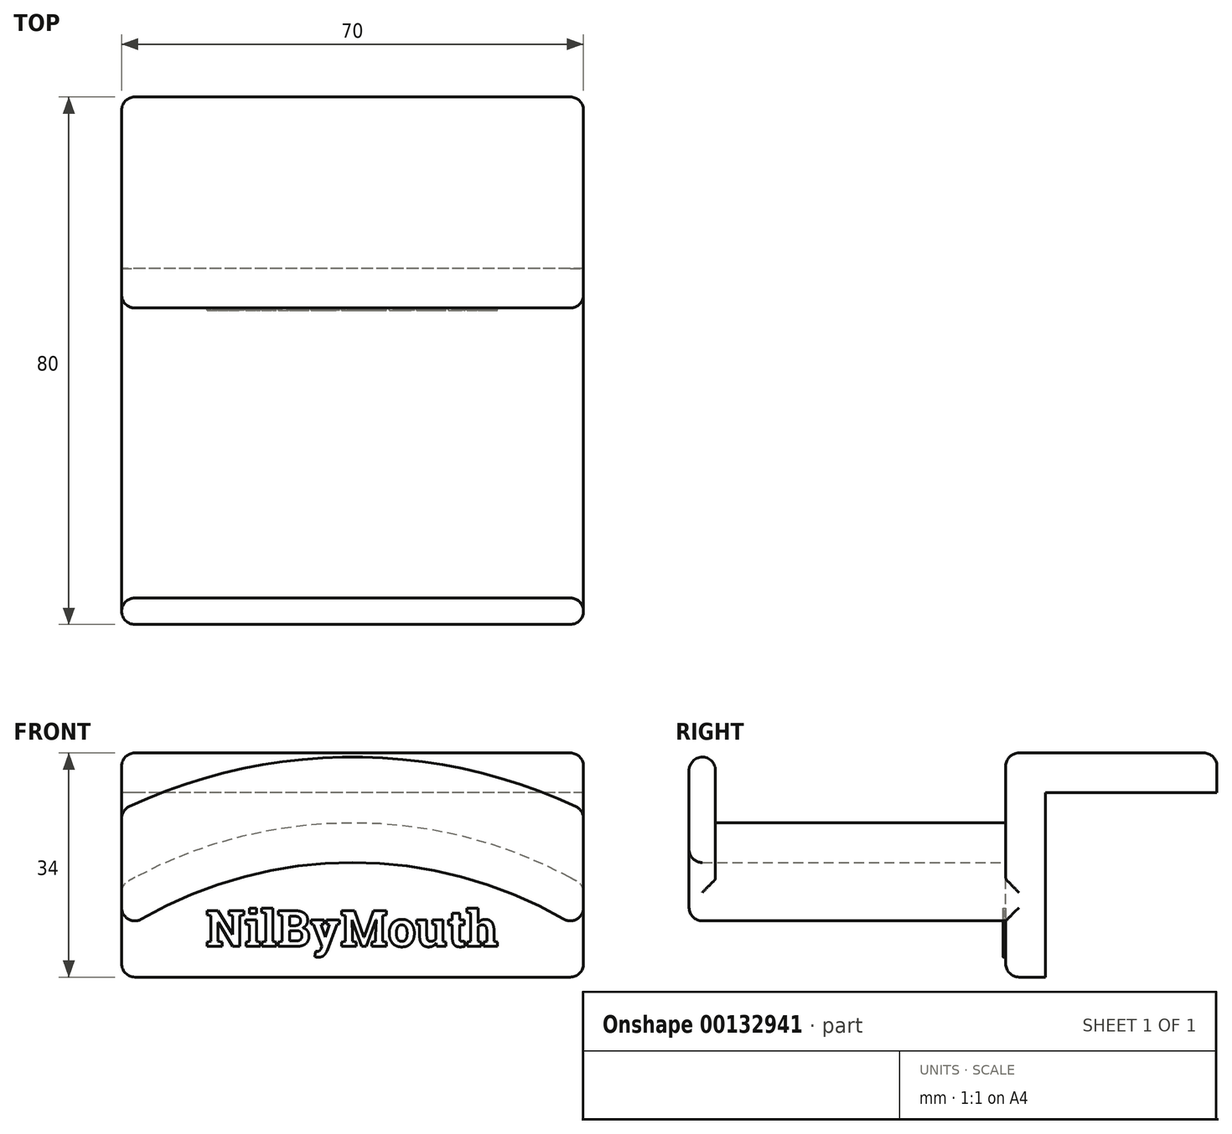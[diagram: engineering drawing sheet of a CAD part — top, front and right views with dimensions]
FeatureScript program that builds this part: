
annotation { "Feature Type Name" : "Feature", "Feature Type Description" : "" }
export const myFeature = defineFeature(function(context is Context, id is Id, definition is map)
    precondition{}
    {
        {
            var Q0;
            Q0=qCreatedBy(makeId("Front.planeOp"),FACE);
            var sketch = newSketch(context, id + "F0", { "sketchPlane" : qUnion([Q0])});
            skLineSegment(sketch, "E0.top", {"start": v(70, 0) * mm, "end": v(0, 0) * mm});
            skLineSegment(sketch, "E0.left", {"start": v(70, 14) * mm, "end": v(70, 0) * mm});
            skLineSegment(sketch, "E0.right", {"start": v(0, 14) * mm, "end": v(0, 0) * mm});
            skArc(sketch, "E1", {"start": v(70, 14) * mm, "mid": v(35, 23.38) * mm, "end": v(0, 14) * mm});
            skArc(sketch, "E2.0", {"start": v(70, 6.96) * mm, "mid": v(35, 17.38) * mm, "end": v(0, 6.96) * mm});
            skLineSegment(sketch, "E3.top", {"start": v(0, 34) * mm, "end": v(70, 34) * mm});
            skLineSegment(sketch, "E3.left", {"start": v(0, 14) * mm, "end": v(0, 34) * mm});
            skLineSegment(sketch, "E3.right", {"start": v(70, 14) * mm, "end": v(70, 34) * mm});
            skSolve(sketch);
        }
        {
            var Q0;
            Q0 = qSketchRegion(id + "F0", true);
            extrude(context, id + "F1", {"entities" : qUnion([Q0]), "depth" : 6 * mm});
        }
        {
            var Q0;
            {var subQ0=sQuery(id+"F0.wireOp",EDGE,"E1");Q0=makeQuery(id+"F0.imprint","IMPRINT",FACE,{"disambiguationData":[TD([[makeQuery(id+"F0.imprint","IMPRINT",EDGE,{"derivedFrom":subQ0}),1.0]])]});}
            extrude(context, id + "F2", {"entities" : qUnion([Q0]), "operationType" : NewBodyOperationType.ADD, "depth" : 50 * mm});
        }
        {
            var Q0;
            Q0=makeQuery(id+"F2.opExtrude","CAP_FACE",FACE,{"disambiguationData":[OSD([sQuery(id+"F0.wireOp",EDGE,"E0.left"),sQuery(id+"F0.wireOp",EDGE,"E0.right"),sQuery(id+"F0.wireOp",EDGE,"E1"),sQuery(id+"F0.wireOp",EDGE,"E2.0")])],"isStart":false});
            var sketch = newSketch(context, id + "F3", { "sketchPlane" : qUnion([Q0])});
            skArc(sketch, "E4.0", {"start": v(70, 25.32) * mm, "mid": v(35, 33.38) * mm, "end": v(0, 25.32) * mm});
            skLineSegment(sketch, "E5", {"start": v(0, 14) * mm, "end": v(0, 25.32) * mm});
            skLineSegment(sketch, "E6", {"start": v(70, 14) * mm, "end": v(70, 25.32) * mm});
            skSolve(sketch);
        }
        {
            var Q0;
            Q0 = qSketchRegion(id + "F3", true);
            var Q1;
            Q1=makeQuery(id+"F3.imprint","IMPRINT",FACE,{"disambiguationData":[TD([[makeQuery(id+"F3.imprint","IMPRINT",EDGE,{"derivedFrom":makeQuery(id+"F2.opExtrude","CAP_EDGE",EDGE,{"disambiguationData":[OSD([sQuery(id+"F0.wireOp",EDGE,"E0.left")])],"isStart":false})}),-1.0]])]});
            var Q2;
            Q2=makeQuery(id+"F3.imprint","IMPRINT",FACE,{"disambiguationData":[TD([[makeQuery(id+"F3.imprint","IMPRINT",EDGE,{"derivedFrom":sQuery(id+"F3.wireOp",EDGE,"E4.0")}),1.0]])]});
            extrude(context, id + "F4", {"entities" : qUnion([Q0, Q1, Q2]), "operationType" : NewBodyOperationType.ADD, "depth" : 4 * mm});
        }
        {
            var Q0;
            {var subQ0=sQuery(id+"F0.wireOp",EDGE,"E0.left");var subQ1=sQuery(id+"F0.wireOp",EDGE,"E3.left");var subQ2=sQuery(id+"F0.wireOp",EDGE,"E0.right");var subQ3=sQuery(id+"F0.wireOp",EDGE,"E3.right");var subQ4=sQuery(id+"F0.wireOp",EDGE,"E0.top");Q0=makeQuery(id+"F2.boolean.opBoolean","SPLIT",FACE,{"disambiguationData":[TD([makeQuery(id+"F1.opExtrude","SWEPT_FACE",FACE,{"disambiguationData":[OSD([subQ4])]})])],"derivedFrom":makeQuery(id+"F1.opExtrude","CAP_FACE",FACE,{"disambiguationData":[OSD([subQ4,subQ0,subQ2,sQuery(id+"F0.wireOp",EDGE,"E3.top"),subQ1,subQ3])],"isStart":false})});}
            var sketch = newSketch(context, id + "F5", { "sketchPlane" : qUnion([Q0])});
            skText(sketch, "E7", { "text": "NilByMouth", "fontName": "RobotoSlab-Bold.ttf"});
            const initialGuessF5  = {"E7": [0.01275, 0.00465, 1, 0, 0.0055]};
            skSetInitialGuess(sketch, initialGuessF5);
            skSolve(sketch);
        }
        {
            var Q0;
            Q0 = qSketchRegion(id + "F5", true);
            extrude(context, id + "F6", {"entities" : qUnion([Q0]), "operationType" : NewBodyOperationType.ADD, "depth" : 0.4 * mm});
        }
        {
            var Q0;
            Q0=makeQuery(id+"F1.opExtrude","CAP_FACE",FACE,{"disambiguationData":[OSD([sQuery(id+"F0.wireOp",EDGE,"E0.top"),sQuery(id+"F0.wireOp",EDGE,"E0.left"),sQuery(id+"F0.wireOp",EDGE,"E0.right"),sQuery(id+"F0.wireOp",EDGE,"E3.top"),sQuery(id+"F0.wireOp",EDGE,"E3.left"),sQuery(id+"F0.wireOp",EDGE,"E3.right")])],"isStart":true});
            var sketch = newSketch(context, id + "F7", { "sketchPlane" : qUnion([Q0])});
            skLineSegment(sketch, "E8.bottom", {"start": v(-70, 34) * mm, "end": v(0, 34) * mm});
            skLineSegment(sketch, "E8.top", {"start": v(-70, 28) * mm, "end": v(0, 28) * mm});
            skLineSegment(sketch, "E8.left", {"start": v(-70, 34) * mm, "end": v(-70, 28) * mm});
            skLineSegment(sketch, "E8.right", {"start": v(0, 34) * mm, "end": v(0, 28) * mm});
            skSolve(sketch);
        }
        {
            var Q0;
            Q0 = qSketchRegion(id + "F7", true);
            extrude(context, id + "F8", {"entities" : qUnion([Q0]), "operationType" : NewBodyOperationType.ADD, "depth" : 26 * mm});
        }
        {
            var Q0;
            {var subQ0=sQuery(id+"F0.wireOp",EDGE,"E1");var subQ1=sQuery(id+"F0.wireOp",EDGE,"E0.left");Q0=makeQuery(id+"F2.boolean.opBoolean","MERGE",EDGE,{"derivedFrom":[makeQuery(id+"F1.opExtrude","SWEPT_EDGE",EDGE,{"disambiguationData":[OSD([subQ1,subQ0])]}),makeQuery(id+"F2.opExtrude","SWEPT_EDGE",EDGE,{"disambiguationData":[OSD([subQ1,subQ0])]})]});}
            var Q1;
            {var subQ0=sQuery(id+"F0.wireOp",EDGE,"E1");var subQ1=sQuery(id+"F0.wireOp",EDGE,"E0.right");Q1=makeQuery(id+"F2.boolean.opBoolean","MERGE",EDGE,{"derivedFrom":[makeQuery(id+"F1.opExtrude","SWEPT_EDGE",EDGE,{"disambiguationData":[OSD([subQ1,subQ0])]}),makeQuery(id+"F2.opExtrude","SWEPT_EDGE",EDGE,{"disambiguationData":[OSD([subQ1,subQ0])]})]});}
            var Q2;
            {var subQ0=sQuery(id+"F0.wireOp",EDGE,"E2.0");var subQ1=sQuery(id+"F0.wireOp",EDGE,"E0.left");Q2=makeQuery(id+"F4.boolean.opBoolean","MERGE",EDGE,{"derivedFrom":[makeQuery(id+"F2.opExtrude","SWEPT_EDGE",EDGE,{"disambiguationData":[OSD([subQ1,subQ0])]}),makeQuery(id+"F4.opExtrude","SWEPT_EDGE",EDGE,{"disambiguationData":[OSD([subQ1,subQ0])]})]});}
            var Q3;
            Q3=makeQuery(id+"F1.opExtrude","CAP_EDGE",EDGE,{"disambiguationData":[OSD([sQuery(id+"F0.wireOp",EDGE,"E0.left")])],"isStart":false});
            var Q4;
            Q4=makeQuery(id+"F1.opExtrude","SWEPT_EDGE",EDGE,{"disambiguationData":[OSD([sQuery(id+"F0.wireOp",EDGE,"E0.top"),sQuery(id+"F0.wireOp",EDGE,"E0.left")])]});
            var Q5;
            Q5=makeQuery(id+"F1.opExtrude","CAP_EDGE",EDGE,{"disambiguationData":[OSD([sQuery(id+"F0.wireOp",EDGE,"E0.top")])],"isStart":false});
            var Q6;
            Q6=makeQuery(id+"F1.opExtrude","CAP_EDGE",EDGE,{"disambiguationData":[OSD([sQuery(id+"F0.wireOp",EDGE,"E0.right")])],"isStart":false});
            var Q7;
            {var subQ0=sQuery(id+"F0.wireOp",EDGE,"E2.0");var subQ1=sQuery(id+"F0.wireOp",EDGE,"E0.right");Q7=makeQuery(id+"F4.boolean.opBoolean","MERGE",EDGE,{"derivedFrom":[makeQuery(id+"F2.opExtrude","SWEPT_EDGE",EDGE,{"disambiguationData":[OSD([subQ1,subQ0])]}),makeQuery(id+"F4.opExtrude","SWEPT_EDGE",EDGE,{"disambiguationData":[OSD([subQ1,subQ0])]})]});}
            var Q8;
            Q8=makeQuery(id+"F4.opExtrude","CAP_EDGE",EDGE,{"disambiguationData":[OSD([sQuery(id+"F0.wireOp",EDGE,"E2.0")])],"isStart":false});
            var Q9;
            Q9=makeQuery(id+"F4.opExtrude","CAP_EDGE",EDGE,{"disambiguationData":[OSD([sQuery(id+"F0.wireOp",EDGE,"E0.right"),sQuery(id+"F3.wireOp",EDGE,"E5")])],"isStart":true});
            var Q10;
            Q10=makeQuery(id+"F4.opExtrude","CAP_EDGE",EDGE,{"disambiguationData":[OSD([sQuery(id+"F0.wireOp",EDGE,"E0.right"),sQuery(id+"F3.wireOp",EDGE,"E5")])],"isStart":false});
            var Q11;
            Q11=makeQuery(id+"F4.opExtrude","CAP_EDGE",EDGE,{"disambiguationData":[OSD([sQuery(id+"F0.wireOp",EDGE,"E0.left"),sQuery(id+"F3.wireOp",EDGE,"E6")])],"isStart":false});
            var Q12;
            Q12=makeQuery(id+"F4.opExtrude","CAP_EDGE",EDGE,{"disambiguationData":[OSD([sQuery(id+"F0.wireOp",EDGE,"E0.left"),sQuery(id+"F3.wireOp",EDGE,"E6")])],"isStart":true});
            var Q13;
            Q13=makeQuery(id+"F4.opExtrude","CAP_EDGE",EDGE,{"disambiguationData":[OSD([sQuery(id+"F3.wireOp",EDGE,"E4.0")])],"isStart":true});
            var Q14;
            Q14=makeQuery(id+"F4.opExtrude","CAP_EDGE",EDGE,{"disambiguationData":[OSD([sQuery(id+"F3.wireOp",EDGE,"E4.0")])],"isStart":false});
            var Q15;
            Q15=makeQuery(id+"F4.opExtrude","SWEPT_EDGE",EDGE,{"disambiguationData":[OSD([sQuery(id+"F3.wireOp",EDGE,"E4.0"),sQuery(id+"F3.wireOp",EDGE,"E6")])]});
            var Q16;
            Q16=makeQuery(id+"F4.opExtrude","SWEPT_EDGE",EDGE,{"disambiguationData":[OSD([sQuery(id+"F3.wireOp",EDGE,"E4.0"),sQuery(id+"F3.wireOp",EDGE,"E5")])]});
            var Q17;
            Q17=makeQuery(id+"F1.opExtrude","CAP_EDGE",EDGE,{"disambiguationData":[OSD([sQuery(id+"F0.wireOp",EDGE,"E3.top")])],"isStart":false});
            var Q18;
            Q18=makeQuery(id+"F8.boolean.opBoolean","MERGE",EDGE,{"derivedFrom":[makeQuery(id+"F1.opExtrude","SWEPT_EDGE",EDGE,{"disambiguationData":[OSD([sQuery(id+"F0.wireOp",EDGE,"E3.top"),sQuery(id+"F0.wireOp",EDGE,"E3.right")])]}),makeQuery(id+"F8.opExtrude","SWEPT_EDGE",EDGE,{"disambiguationData":[OSD([sQuery(id+"F7.wireOp",EDGE,"E8.bottom"),sQuery(id+"F7.wireOp",EDGE,"E8.left")])]})]});
            var Q19;
            Q19=makeQuery(id+"F8.opExtrude","CAP_EDGE",EDGE,{"disambiguationData":[OSD([sQuery(id+"F7.wireOp",EDGE,"E8.left")])],"isStart":false});
            var Q20;
            Q20=makeQuery(id+"F8.opExtrude","CAP_EDGE",EDGE,{"disambiguationData":[OSD([sQuery(id+"F7.wireOp",EDGE,"E8.bottom")])],"isStart":false});
            var Q21;
            Q21=makeQuery(id+"F8.boolean.opBoolean","MERGE",EDGE,{"derivedFrom":[makeQuery(id+"F1.opExtrude","SWEPT_EDGE",EDGE,{"disambiguationData":[OSD([sQuery(id+"F0.wireOp",EDGE,"E3.top"),sQuery(id+"F0.wireOp",EDGE,"E3.left")])]}),makeQuery(id+"F8.opExtrude","SWEPT_EDGE",EDGE,{"disambiguationData":[OSD([sQuery(id+"F7.wireOp",EDGE,"E8.bottom"),sQuery(id+"F7.wireOp",EDGE,"E8.right")])]})]});
            var Q22;
            Q22=makeQuery(id+"F8.opExtrude","CAP_EDGE",EDGE,{"disambiguationData":[OSD([sQuery(id+"F7.wireOp",EDGE,"E8.right")])],"isStart":false});
            fillet(context, id + "F9", {"entities" : qUnion([Q0, Q1, Q2, Q3, Q4, Q5, Q6, Q7, Q8, Q9, Q10, Q11, Q12, Q13, Q14, Q15, Q16, Q17, Q18, Q19, Q20, Q21, Q22]), "radius" : 2 * mm, "tangentPropagation" : true, "allowEdgeOverflow" : false});
        }
    });
